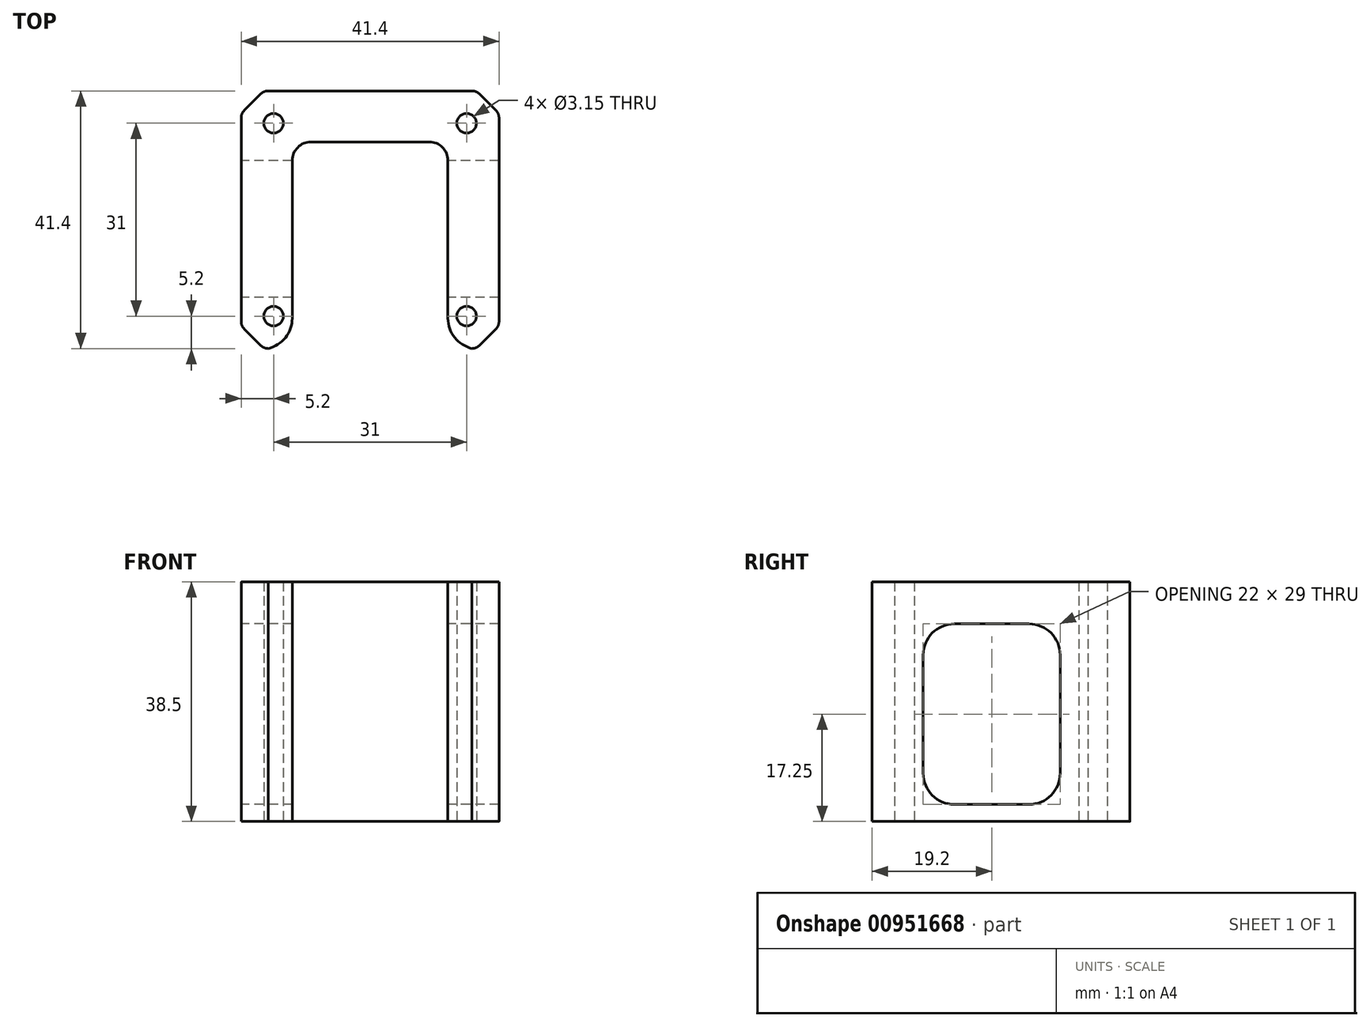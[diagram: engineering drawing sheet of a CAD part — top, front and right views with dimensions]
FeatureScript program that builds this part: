
annotation { "Feature Type Name" : "Feature", "Feature Type Description" : "" }
export const myFeature = defineFeature(function(context is Context, id is Id, definition is map)
    precondition{}
    {
        {
            var Q0;
            Q0=qCreatedBy(makeId("Top.planeOp"),FACE);
            var sketch = newSketch(context, id + "F0", { "sketchPlane" : qUnion([Q0])});
            skLineSegment(sketch, "E0", {"start": v(-5.2, 31.87) * mm, "end": v(-5.2, -0.87) * mm});
            skLineSegment(sketch, "E1", {"start": v(-4.7, -2.07) * mm, "end": v(-2.07, -4.7) * mm});
            skLineSegment(sketch, "E2", {"start": v(33.07, -4.7) * mm, "end": v(35.7, -2.07) * mm});
            skLineSegment(sketch, "E3", {"start": v(36.2, -0.87) * mm, "end": v(36.2, 31.87) * mm});
            skLineSegment(sketch, "E4", {"start": v(35.7, 33.07) * mm, "end": v(33.07, 35.7) * mm});
            skLineSegment(sketch, "E5", {"start": v(-4.7, 33.07) * mm, "end": v(-2.07, 35.7) * mm});
            skLineSegment(sketch, "E6", {"start": v(-0.87, 36.2) * mm, "end": v(31.87, 36.2) * mm});
            skArc(sketch, "E7", {"start": v(-2.07, -4.7) * mm, "mid": v(-1.52, -5.07) * mm, "end": v(-0.87, -5.2) * mm});
            skArc(sketch, "E8", {"start": v(-5.2, -0.87) * mm, "mid": v(-5.07, -1.52) * mm, "end": v(-4.7, -2.07) * mm});
            skArc(sketch, "E9", {"start": v(31.87, -5.2) * mm, "mid": v(32.52, -5.07) * mm, "end": v(33.07, -4.7) * mm});
            skArc(sketch, "E10", {"start": v(35.7, -2.07) * mm, "mid": v(36.07, -1.52) * mm, "end": v(36.2, -0.87) * mm});
            skArc(sketch, "E11", {"start": v(33.07, 35.7) * mm, "mid": v(32.52, 36.07) * mm, "end": v(31.87, 36.2) * mm});
            skArc(sketch, "E12", {"start": v(36.2, 31.87) * mm, "mid": v(36.07, 32.52) * mm, "end": v(35.7, 33.07) * mm});
            skArc(sketch, "E13", {"start": v(-4.7, 33.07) * mm, "mid": v(-5.07, 32.52) * mm, "end": v(-5.2, 31.87) * mm});
            skArc(sketch, "E14", {"start": v(-0.87, 36.2) * mm, "mid": v(-1.52, 36.07) * mm, "end": v(-2.07, 35.7) * mm});
            skCircle(sketch, "E15", {"center": v(0, 31) * mm, "radius": 1.57 * mm});
            skCircle(sketch, "E16", {"center": v(31, 31) * mm, "radius": 1.57 * mm});
            skCircle(sketch, "E17", {"center": v(0, 0) * mm, "radius": 1.57 * mm});
            skCircle(sketch, "E18", {"center": v(31, 0) * mm, "radius": 1.57 * mm});
            skPoint(sketch, "E19.centerSnap0", {"position": v(0, 15.5) * mm});
            skPoint(sketch, "E19.centerSnap1", {"position": v(15.5, 31) * mm});
            skLineSegment(sketch, "E20", {"start": v(3, 28) * mm, "end": v(3, -5.2) * mm});
            skLineSegment(sketch, "E21", {"start": v(3, 28) * mm, "end": v(28, 28) * mm});
            skLineSegment(sketch, "E22", {"start": v(28, 28) * mm, "end": v(28, -5.2) * mm});
            skLineSegment(sketch, "E23", {"start": v(-0.87, -5.2) * mm, "end": v(3, -5.2) * mm});
            skLineSegment(sketch, "E24", {"start": v(28, -5.2) * mm, "end": v(31.87, -5.2) * mm});
            skSolve(sketch);
        }
        {
            var Q0;
            Q0=makeQuery(id+"F0.imprint","IMPRINT",FACE,{"disambiguationData":[TD([[makeQuery(id+"F0.imprint","IMPRINT",EDGE,{"derivedFrom":sQuery(id+"F0.wireOp",EDGE,"E0")}),1.0]])]});
            extrude(context, id + "F1", {"entities" : qUnion([Q0]), "depth" : 38.5 * mm, "offsetDistance" : 25 * mm});
        }
        {
            var Q0;
            Q0=makeQuery(id+"F1.opExtrude","SWEPT_FACE",FACE,{"disambiguationData":[OSD([sQuery(id+"F0.wireOp",EDGE,"E0")])]});
            var sketch = newSketch(context, id + "F2", { "sketchPlane" : qUnion([Q0])});
            skLineSegment(sketch, "E25.bottom", {"start": v(-28, 31.75) * mm, "end": v(-3, 31.75) * mm});
            skLineSegment(sketch, "E25.top", {"start": v(-28, 6.75) * mm, "end": v(-3, 6.75) * mm});
            skLineSegment(sketch, "E25.left", {"start": v(-28, 31.75) * mm, "end": v(-28, 6.75) * mm});
            skLineSegment(sketch, "E25.right", {"start": v(-3, 31.75) * mm, "end": v(-3, 6.75) * mm});
            skPoint(sketch, "E25.middle", {"position": v(-15.5, 19.25) * mm});
            skPoint(sketch, "E25.middle.positionSnap0", {"position": v(-15.5, 0) * mm});
            skPoint(sketch, "E25.middle.positionSnap1", {"position": v(-31.87, 19.25) * mm});
            skPoint(sketch, "E25.centerSnap0", {"position": v(-15.5, 0) * mm});
            skPoint(sketch, "E25.centerSnap1", {"position": v(-31.87, 19.25) * mm});
            skLineSegment(sketch, "E26.bottom", {"start": v(-28, 31.75) * mm, "end": v(-25, 31.75) * mm});
            skLineSegment(sketch, "E26.top", {"start": v(-28, 6.75) * mm, "end": v(-25, 6.75) * mm});
            skLineSegment(sketch, "E26.right", {"start": v(-25, 31.75) * mm, "end": v(-25, 6.75) * mm});
            skLineSegment(sketch, "E27.bottom", {"start": v(-25, 6.75) * mm, "end": v(-3, 6.75) * mm});
            skLineSegment(sketch, "E27.top", {"start": v(-25, 2.75) * mm, "end": v(-3, 2.75) * mm});
            skLineSegment(sketch, "E27.left", {"start": v(-25, 6.75) * mm, "end": v(-25, 2.75) * mm});
            skLineSegment(sketch, "E27.right", {"start": v(-3, 6.75) * mm, "end": v(-3, 2.75) * mm});
            skSolve(sketch);
        }
        {
            var Q0;
            {var subQ2=sQuery(id+"F2.wireOp",EDGE,"E25.right");Q0=makeQuery(id+"F2.imprint","IMPRINT",FACE,{"disambiguationData":[TD([[makeQuery(id+"F2.imprint","IMPRINT",EDGE,{"derivedFrom":subQ2}),-1.0]])]});}
            var Q1;
            Q1=makeQuery(id+"F2.imprint","IMPRINT",FACE,{"disambiguationData":[TD([[makeQuery(id+"F2.imprint","IMPRINT",EDGE,{"derivedFrom":sQuery(id+"F2.wireOp",EDGE,"E27.top")}),1.0]])]});
            extrude(context, id + "F3", {"entities" : qUnion([Q0, Q1]), "operationType" : NewBodyOperationType.REMOVE, "oppositeDirection" : true, "depth" : 60 * mm, "offsetDistance" : 25 * mm});
        }
        {
            var Q0;
            {var subQ0=sQuery(id+"F2.wireOp",EDGE,"E27.top");var subQ1=sQuery(id+"F2.wireOp",EDGE,"E27.left");Q0=makeQuery(id+"F3.boolean.opBoolean","COPY",EDGE,{"disambiguationData":[TD([makeQuery(id+"F1.opExtrude","SWEPT_FACE",FACE,{"disambiguationData":[OSD([sQuery(id+"F0.wireOp",EDGE,"E3")])]})])],"derivedFrom":makeQuery(id+"F3.opExtrude","SWEPT_EDGE",EDGE,{"disambiguationData":[OSD([subQ0,subQ1])]})});}
            var Q1;
            {var subQ0=sQuery(id+"F2.wireOp",EDGE,"E27.left");var subQ1=sQuery(id+"F2.wireOp",EDGE,"E27.top");Q1=makeQuery(id+"F3.boolean.opBoolean","COPY",EDGE,{"disambiguationData":[TD([makeQuery(id+"F1.opExtrude","SWEPT_FACE",FACE,{"disambiguationData":[OSD([sQuery(id+"F0.wireOp",EDGE,"E0")])]})])],"derivedFrom":makeQuery(id+"F3.opExtrude","SWEPT_EDGE",EDGE,{"disambiguationData":[OSD([subQ1,subQ0])]})});}
            var Q2;
            {var subQ0=sQuery(id+"F2.wireOp",EDGE,"E27.right");var subQ1=sQuery(id+"F2.wireOp",EDGE,"E27.top");Q2=makeQuery(id+"F3.boolean.opBoolean","COPY",EDGE,{"disambiguationData":[TD([makeQuery(id+"F1.opExtrude","SWEPT_FACE",FACE,{"disambiguationData":[OSD([sQuery(id+"F0.wireOp",EDGE,"E0")])]})])],"derivedFrom":makeQuery(id+"F3.opExtrude","SWEPT_EDGE",EDGE,{"disambiguationData":[OSD([subQ1,subQ0])]})});}
            var Q3;
            {var subQ0=sQuery(id+"F2.wireOp",EDGE,"E27.top");var subQ1=sQuery(id+"F2.wireOp",EDGE,"E27.right");Q3=makeQuery(id+"F3.boolean.opBoolean","COPY",EDGE,{"disambiguationData":[TD([makeQuery(id+"F1.opExtrude","SWEPT_FACE",FACE,{"disambiguationData":[OSD([sQuery(id+"F0.wireOp",EDGE,"E3")])]})])],"derivedFrom":makeQuery(id+"F3.opExtrude","SWEPT_EDGE",EDGE,{"disambiguationData":[OSD([subQ0,subQ1])]})});}
            var Q4;
            {var subQ0=sQuery(id+"F2.wireOp",EDGE,"E25.right");var subQ1=sQuery(id+"F2.wireOp",EDGE,"E25.bottom");Q4=makeQuery(id+"F3.boolean.opBoolean","COPY",EDGE,{"disambiguationData":[TD([makeQuery(id+"F1.opExtrude","SWEPT_FACE",FACE,{"disambiguationData":[OSD([sQuery(id+"F0.wireOp",EDGE,"E0")])]})])],"derivedFrom":makeQuery(id+"F3.opExtrude","SWEPT_EDGE",EDGE,{"disambiguationData":[OSD([subQ1,subQ0])]})});}
            var Q5;
            {var subQ0=sQuery(id+"F2.wireOp",EDGE,"E25.bottom");var subQ1=sQuery(id+"F2.wireOp",EDGE,"E25.right");Q5=makeQuery(id+"F3.boolean.opBoolean","COPY",EDGE,{"disambiguationData":[TD([makeQuery(id+"F1.opExtrude","SWEPT_FACE",FACE,{"disambiguationData":[OSD([sQuery(id+"F0.wireOp",EDGE,"E3")])]})])],"derivedFrom":makeQuery(id+"F3.opExtrude","SWEPT_EDGE",EDGE,{"disambiguationData":[OSD([subQ0,subQ1])]})});}
            var Q6;
            {var subQ0=sQuery(id+"F2.wireOp",EDGE,"E25.bottom");var subQ1=sQuery(id+"F2.wireOp",EDGE,"E26.right");Q6=makeQuery(id+"F3.boolean.opBoolean","COPY",EDGE,{"disambiguationData":[TD([makeQuery(id+"F1.opExtrude","SWEPT_FACE",FACE,{"disambiguationData":[OSD([sQuery(id+"F0.wireOp",EDGE,"E3")])]})])],"derivedFrom":makeQuery(id+"F3.opExtrude","SWEPT_EDGE",EDGE,{"disambiguationData":[OSD([subQ0,subQ1])]})});}
            var Q7;
            {var subQ0=sQuery(id+"F2.wireOp",EDGE,"E25.bottom");var subQ1=sQuery(id+"F2.wireOp",EDGE,"E26.right");Q7=makeQuery(id+"F3.boolean.opBoolean","COPY",EDGE,{"disambiguationData":[TD([makeQuery(id+"F1.opExtrude","SWEPT_FACE",FACE,{"disambiguationData":[OSD([sQuery(id+"F0.wireOp",EDGE,"E0")])]})])],"derivedFrom":makeQuery(id+"F3.opExtrude","SWEPT_EDGE",EDGE,{"disambiguationData":[OSD([subQ0,subQ1])]})});}
            var Q8;
            Q8=makeQuery(id+"F1.opExtrude","SWEPT_EDGE",EDGE,{"disambiguationData":[OSD([sQuery(id+"F0.wireOp",EDGE,"E22"),sQuery(id+"F0.wireOp",EDGE,"E24")])]});
            var Q9;
            Q9=makeQuery(id+"F1.opExtrude","SWEPT_EDGE",EDGE,{"disambiguationData":[OSD([sQuery(id+"F0.wireOp",EDGE,"E20"),sQuery(id+"F0.wireOp",EDGE,"E23")])]});
            fillet(context, id + "F4", {"entities" : qUnion([Q0, Q1, Q2, Q3, Q4, Q5, Q6, Q7, Q8, Q9]), "radius" : 5 * mm, "tangentPropagation" : true, "allowEdgeOverflow" : false});
        }
        {
            var Q0;
            Q0=makeQuery(id+"F1.opExtrude","SWEPT_EDGE",EDGE,{"disambiguationData":[OSD([sQuery(id+"F0.wireOp",EDGE,"E21"),sQuery(id+"F0.wireOp",EDGE,"E22")])]});
            var Q1;
            Q1=makeQuery(id+"F1.opExtrude","SWEPT_EDGE",EDGE,{"disambiguationData":[OSD([sQuery(id+"F0.wireOp",EDGE,"E20"),sQuery(id+"F0.wireOp",EDGE,"E21")])]});
            fillet(context, id + "F5", {"entities" : qUnion([Q0, Q1]), "radius" : 3 * mm, "tangentPropagation" : true, "allowEdgeOverflow" : false});
        }
    });
